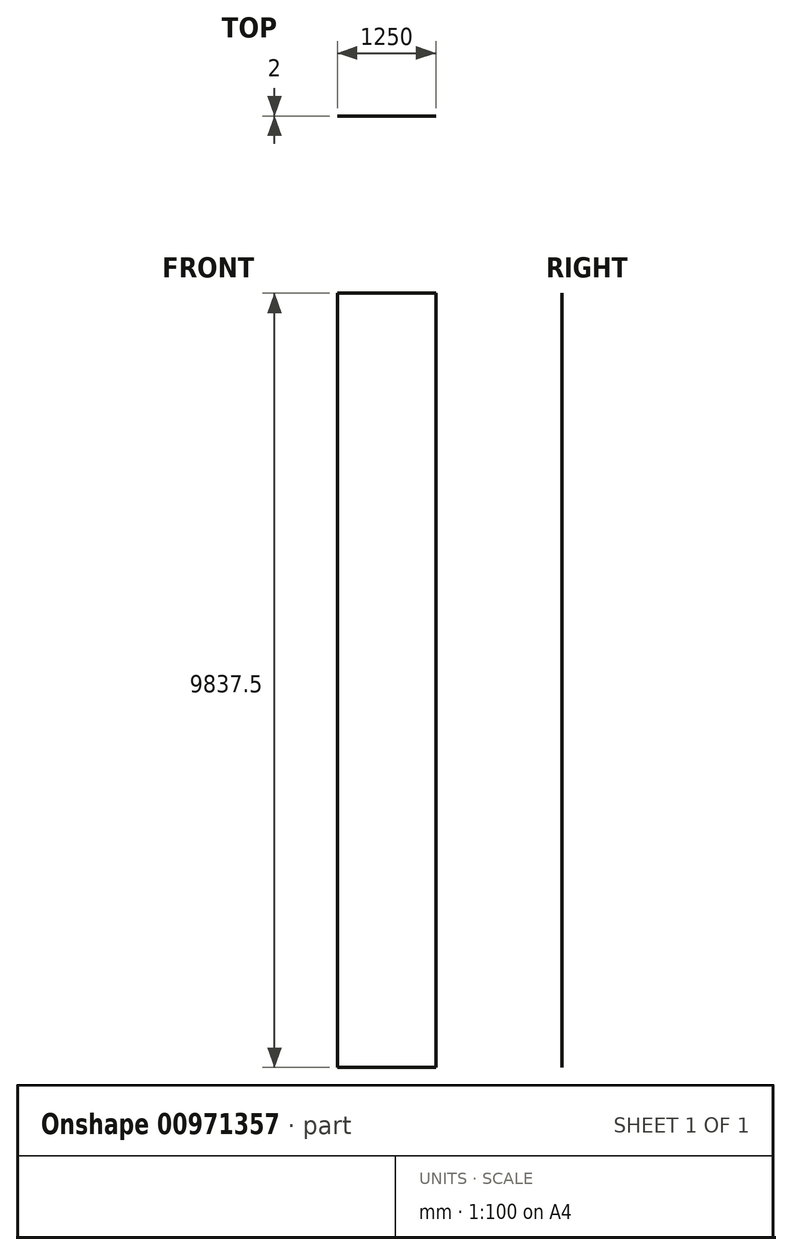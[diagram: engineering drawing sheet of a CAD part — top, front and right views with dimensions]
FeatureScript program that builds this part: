
annotation { "Feature Type Name" : "Feature", "Feature Type Description" : "" }
export const myFeature = defineFeature(function(context is Context, id is Id, definition is map)
    precondition{}
    {
        {
            var Q0;
            Q0=qCreatedBy(makeId("Front.planeOp"),FACE);
            var sketch = newSketch(context, id + "F0", { "sketchPlane" : qUnion([Q0])});
            skLineSegment(sketch, "E0.bottom", {"start": v(625, 4918.75) * mm, "end": v(-625, 4918.75) * mm});
            skLineSegment(sketch, "E0.top", {"start": v(625, -4918.75) * mm, "end": v(-625, -4918.75) * mm});
            skLineSegment(sketch, "E0.left", {"start": v(625, 4918.75) * mm, "end": v(625, -4918.75) * mm});
            skLineSegment(sketch, "E0.right", {"start": v(-625, 4918.75) * mm, "end": v(-625, -4918.75) * mm});
            skPoint(sketch, "E0.middle", {"position": v(0, 0) * mm});
            skSolve(sketch);
        }
        {
            var Q0;
            Q0=makeQuery(id+"F0.imprint","IMPRINT",FACE,{"disambiguationData":[TD([[makeQuery(id+"F0.imprint","IMPRINT",EDGE,{"derivedFrom":sQuery(id+"F0.wireOp",EDGE,"E0.bottom")}),1.0]])]});
            extrude(context, id + "F1", {"entities" : qUnion([Q0]), "depth" : 2 * mm, "offsetDistance" : 25 * mm});
        }
    });
